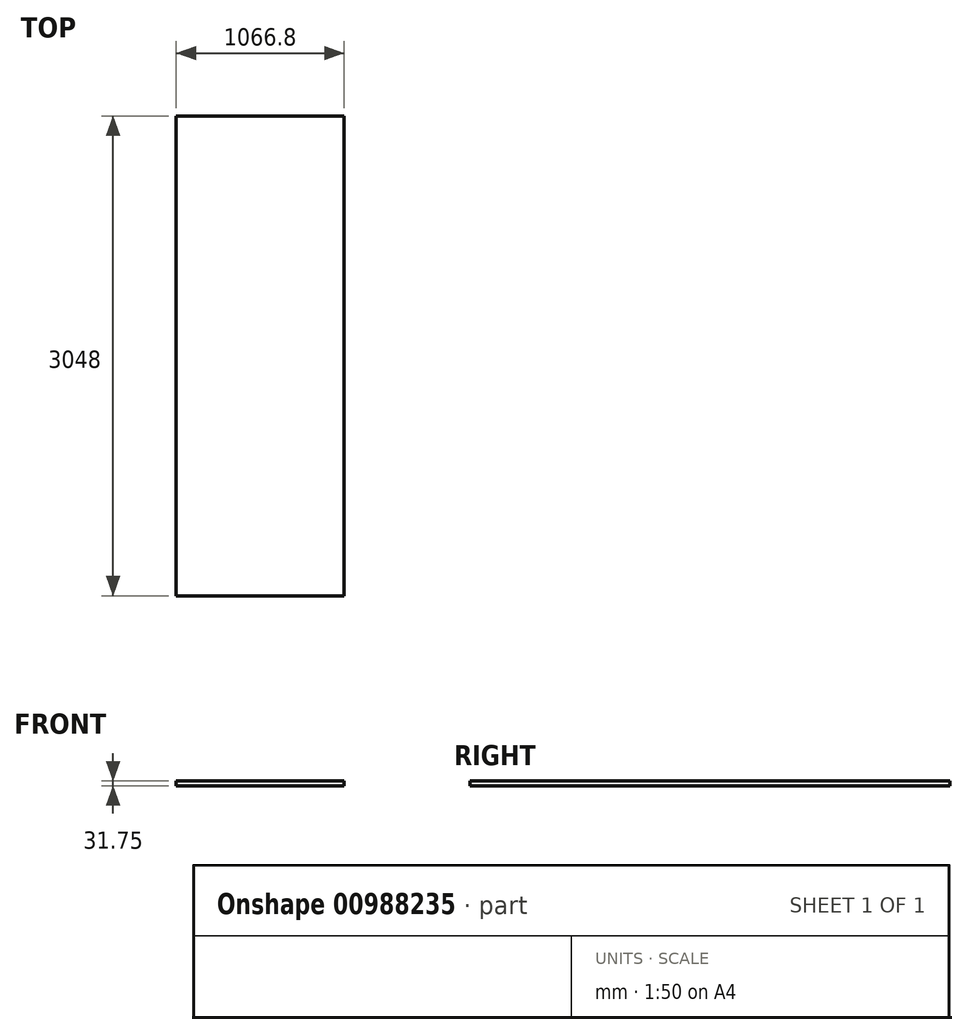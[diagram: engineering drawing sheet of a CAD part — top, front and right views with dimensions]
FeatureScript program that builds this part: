
annotation { "Feature Type Name" : "Feature", "Feature Type Description" : "" }
export const myFeature = defineFeature(function(context is Context, id is Id, definition is map)
    precondition{}
    {
        {
            var Q0;
            Q0=qCreatedBy(makeId("Top.planeOp"),FACE);
            var sketch = newSketch(context, id + "F0", { "sketchPlane" : qUnion([Q0])});
            skLineSegment(sketch, "E0.bottom", {"start": v(0, 0) * mm, "end": v(-1066.8, 0) * mm});
            skLineSegment(sketch, "E0.top", {"start": v(0, 3048) * mm, "end": v(-1066.8, 3048) * mm});
            skLineSegment(sketch, "E0.left", {"start": v(0, 0) * mm, "end": v(0, 3048) * mm});
            skLineSegment(sketch, "E0.right", {"start": v(-1066.8, 0) * mm, "end": v(-1066.8, 3048) * mm});
            skSolve(sketch);
        }
        {
            var Q0;
            Q0 = qSketchRegion(id + "F0", true);
            extrude(context, id + "F1", {"entities" : qUnion([Q0]), "depth" : 31.75 * mm, "offsetDistance" : 25.4 * mm});
        }
    });
